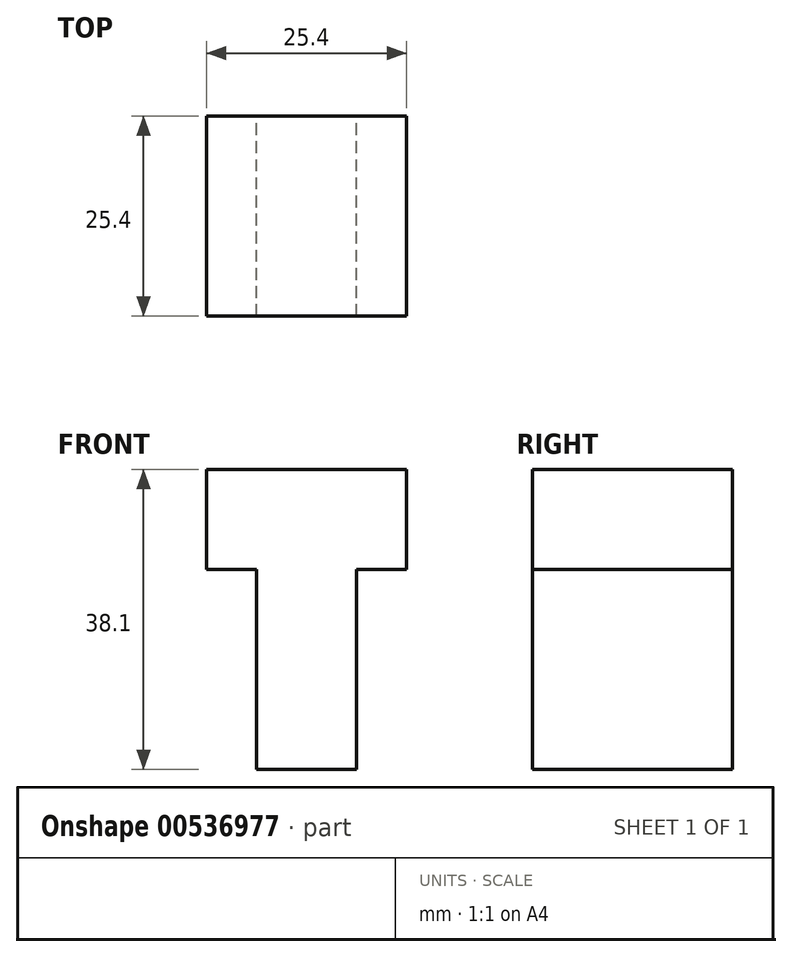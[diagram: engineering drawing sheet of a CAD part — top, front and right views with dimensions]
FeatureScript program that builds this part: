
annotation { "Feature Type Name" : "Feature", "Feature Type Description" : "" }
export const myFeature = defineFeature(function(context is Context, id is Id, definition is map)
    precondition{}
    {
        {
            var Q0;
            Q0=qCreatedBy(makeId("Front.planeOp"),FACE);
            var sketch = newSketch(context, id + "F0", { "sketchPlane" : qUnion([Q0])});
            skLineSegment(sketch, "E0", {"start": v(-50.98, 49.67) * mm, "end": v(-50.98, 24.27) * mm});
            skLineSegment(sketch, "E1", {"start": v(-50.98, 24.27) * mm, "end": v(-38.28, 24.27) * mm});
            skLineSegment(sketch, "E2", {"start": v(-38.28, 24.27) * mm, "end": v(-38.28, 49.67) * mm});
            skLineSegment(sketch, "E3", {"start": v(-38.28, 49.67) * mm, "end": v(-31.93, 49.67) * mm});
            skLineSegment(sketch, "E4", {"start": v(-31.93, 49.67) * mm, "end": v(-31.93, 62.37) * mm});
            skLineSegment(sketch, "E5", {"start": v(-31.93, 62.37) * mm, "end": v(-57.33, 62.37) * mm});
            skLineSegment(sketch, "E6", {"start": v(-57.33, 62.37) * mm, "end": v(-57.33, 49.67) * mm});
            skLineSegment(sketch, "E7", {"start": v(-57.33, 49.67) * mm, "end": v(-50.98, 49.67) * mm});
            skSolve(sketch);
        }
        {
            var Q0;
            Q0=makeQuery(id+"F0.imprint","IMPRINT",FACE,{"disambiguationData":[TD([[makeQuery(id+"F0.imprint","IMPRINT",EDGE,{"derivedFrom":sQuery(id+"F0.wireOp",EDGE,"E0")}),1.0]])]});
            extrude(context, id + "F1", {"entities" : qUnion([Q0]), "depth" : 25.4 * mm, "offsetDistance" : 25.4 * mm});
        }
    });
